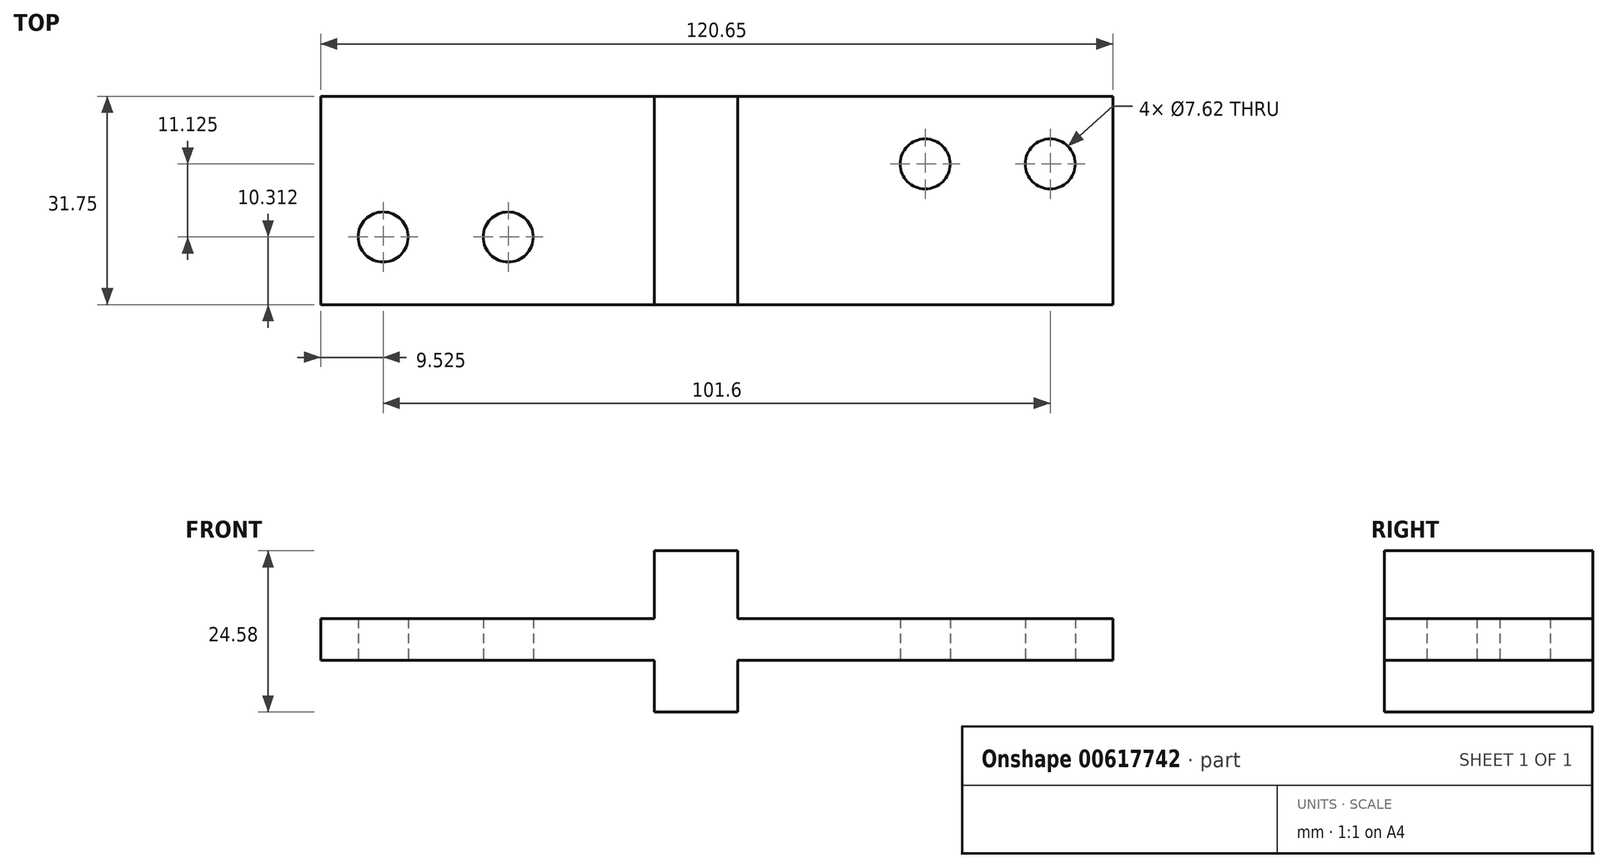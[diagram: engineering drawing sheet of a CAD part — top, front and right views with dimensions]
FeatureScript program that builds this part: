
annotation { "Feature Type Name" : "Feature", "Feature Type Description" : "" }
export const myFeature = defineFeature(function(context is Context, id is Id, definition is map)
    precondition{}
    {
        {
            var Q0;
            Q0=qCreatedBy(makeId("Front.planeOp"),FACE);
            var sketch = newSketch(context, id + "F0", { "sketchPlane" : qUnion([Q0])});
            skLineSegment(sketch, "E0", {"start": v(0, 0) * mm, "end": v(50.8, 0) * mm});
            skLineSegment(sketch, "E1", {"start": v(50.8, 0) * mm, "end": v(50.8, -7.92) * mm});
            skLineSegment(sketch, "E2", {"start": v(50.8, -7.92) * mm, "end": v(63.5, -7.92) * mm});
            skLineSegment(sketch, "E3", {"start": v(63.5, -7.92) * mm, "end": v(63.5, 0) * mm});
            skLineSegment(sketch, "E4", {"start": v(63.5, 0) * mm, "end": v(120.65, 0) * mm});
            skLineSegment(sketch, "E5", {"start": v(120.65, 0) * mm, "end": v(120.65, 6.35) * mm});
            skLineSegment(sketch, "E6", {"start": v(120.65, 6.35) * mm, "end": v(63.5, 6.35) * mm});
            skLineSegment(sketch, "E7", {"start": v(63.5, 6.35) * mm, "end": v(63.5, 16.66) * mm});
            skLineSegment(sketch, "E8", {"start": v(63.5, 16.66) * mm, "end": v(50.8, 16.66) * mm});
            skLineSegment(sketch, "E9", {"start": v(50.8, 16.66) * mm, "end": v(50.8, 6.35) * mm});
            skLineSegment(sketch, "E10", {"start": v(50.8, 6.35) * mm, "end": v(0, 6.35) * mm});
            skLineSegment(sketch, "E11", {"start": v(0, 6.35) * mm, "end": v(0, 0) * mm});
            skSolve(sketch);
        }
        {
            var Q0;
            Q0 = qSketchRegion(id + "F0", true);
            extrude(context, id + "F1", {"entities" : qUnion([Q0]), "depth" : 31.75 * mm, "offsetDistance" : 25.4 * mm});
        }
        {
            var Q0;
            Q0=makeQuery(id+"F1.opExtrude","SWEPT_FACE",FACE,{"disambiguationData":[OSD([sQuery(id+"F0.wireOp",EDGE,"E0")])]});
            var sketch = newSketch(context, id + "F2", { "sketchPlane" : qUnion([Q0])});
            skCircle(sketch, "E12", {"center": v(111.12, 10.31) * mm, "radius": 3.81 * mm});
            skCircle(sketch, "E13", {"center": v(92.08, 10.31) * mm, "radius": 3.81 * mm});
            skCircle(sketch, "E14", {"center": v(9.53, 21.44) * mm, "radius": 3.81 * mm});
            skCircle(sketch, "E15", {"center": v(28.57, 21.44) * mm, "radius": 3.81 * mm});
            skSolve(sketch);
        }
        {
            var Q0;
            Q0=sQuery(id+"F2.wireOp",VERTEX,"E14.center");
            var Q1;
            Q1=sQuery(id+"F2.wireOp",VERTEX,"E15.center");
            var Q2;
            Q2=sQuery(id+"F2.wireOp",VERTEX,"E13.center");
            var Q3;
            Q3=sQuery(id+"F2.wireOp",VERTEX,"E12.center");
            var Q4;
            Q4=makeQuery(id+"F1.opExtrude","SWEPT_BODY",BODY,{"disambiguationData":[OSD([sQuery(id+"F0.wireOp",EDGE,"E0"),sQuery(id+"F0.wireOp",EDGE,"E1"),sQuery(id+"F0.wireOp",EDGE,"E2"),sQuery(id+"F0.wireOp",EDGE,"E3"),sQuery(id+"F0.wireOp",EDGE,"E4"),sQuery(id+"F0.wireOp",EDGE,"E5"),sQuery(id+"F0.wireOp",EDGE,"E6"),sQuery(id+"F0.wireOp",EDGE,"E7"),sQuery(id+"F0.wireOp",EDGE,"E8"),sQuery(id+"F0.wireOp",EDGE,"E9"),sQuery(id+"F0.wireOp",EDGE,"E10"),sQuery(id+"F0.wireOp",EDGE,"E11")])]});
            hole(context, id + "F3", {"style" : HoleStyle.SIMPLE, "endStyle" : HoleEndStyle.THROUGH, "holeDiameter" : 7.62 * mm, "majorDiameter" : 6.35 * mm, "isTappedThrough" : true, "tappedDepth" : 12.7 * mm, "tapClearance" : 3, "locations" : qUnion([Q0, Q1, Q2, Q3]), "scope" : qUnion([Q4])});
        }
    });
